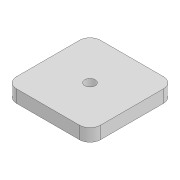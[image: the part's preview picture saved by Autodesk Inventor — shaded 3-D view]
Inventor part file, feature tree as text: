
AUTODESK INVENTOR PART (.ipt)
format: ipt  version: 2020 (Build 240168000, 168)  size: 88,576 bytes
history: native  units: mm
features: other x1, extrude x1, fillet x1, sketch x1
ambient origin geometry x8: Origin, YZ Plane, XZ Plane, XY Plane, X Axis, Y Axis, Z Axis, Center Point
bodies: Body1 (feature_tree)
feature tree (4):
  other  "Sólido1"
  extrude  "Extrusão1"  Depth=80.0mm
  fillet  "Arredondamento1"  Radius=10.0mm
  sketch  "Esboço1"  dims[d0=80.0mm d1=80.0mm d2=10.0mm d3=12.0mm d4=0.0mm d5=10.0mm]
